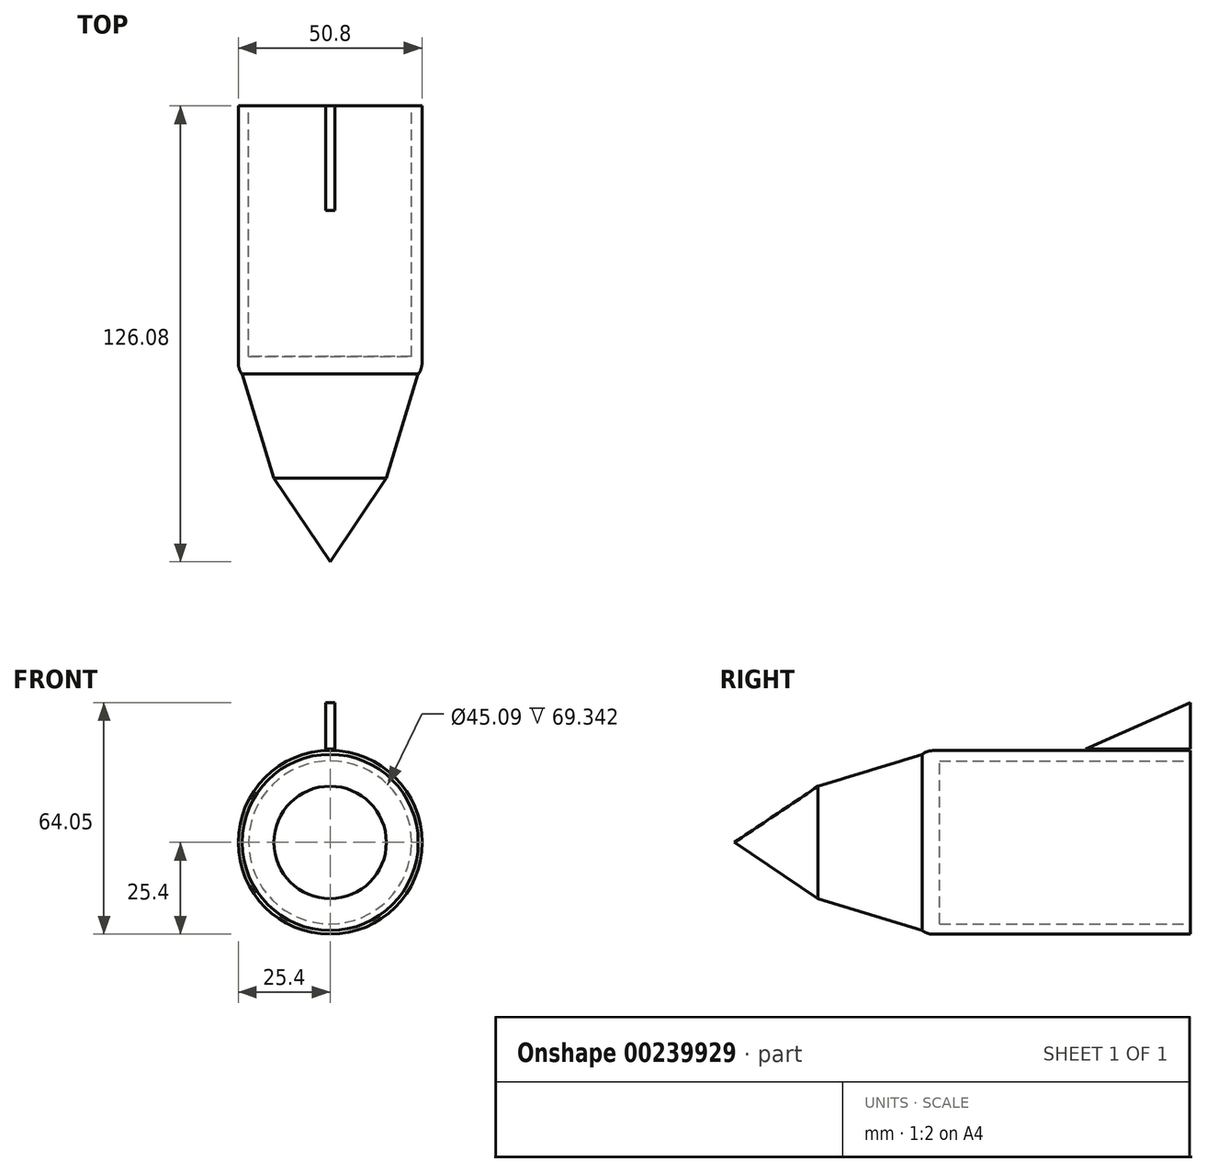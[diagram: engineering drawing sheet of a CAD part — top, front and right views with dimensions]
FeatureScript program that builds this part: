
annotation { "Feature Type Name" : "Feature", "Feature Type Description" : "" }
export const myFeature = defineFeature(function(context is Context, id is Id, definition is map)
    precondition{}
    {
        {
            var Q0;
            Q0=qCreatedBy(makeId("Front.planeOp"),FACE);
            var sketch = newSketch(context, id + "F0", { "sketchPlane" : qUnion([Q0])});
            skCircle(sketch, "E0", {"center": v(0, 0) * mm, "radius": 25.4 * mm});
            skSolve(sketch);
        }
        {
            var Q0;
            Q0 = qSketchRegion(id + "F0", true);
            extrude(context, id + "F1", {"entities" : qUnion([Q0]), "depth" : 76.2 * mm});
        }
        {
            var Q0;
            Q0=qCreatedBy(makeId("Front.planeOp"),FACE);
            var sketch = newSketch(context, id + "F2", { "sketchPlane" : qUnion([Q0])});
            skCircle(sketch, "E1", {"center": v(0, 0) * mm, "radius": 22.55 * mm});
            skSolve(sketch);
        }
        {
            var Q0;
            Q0 = qSketchRegion(id + "F2", true);
            extrude(context, id + "F3", {"entities" : qUnion([Q0]), "operationType" : NewBodyOperationType.REMOVE, "depth" : 69.34 * mm});
        }
        {
            var Q0;
            Q0=makeQuery(id+"F1.opExtrude","CAP_EDGE",EDGE,{"disambiguationData":[OSD([sQuery(id+"F0.wireOp",EDGE,"E0")])],"isStart":false});
            fillet(context, id + "F4", {"entities" : qUnion([Q0]), "radius" : 5.08 * mm, "tangentPropagation" : true, "allowEdgeOverflow" : false});
        }
        {
            var Q0;
            Q0=qCreatedBy(makeId("Right.planeOp"),FACE);
            var sketch = newSketch(context, id + "F5", { "sketchPlane" : qUnion([Q0])});
            skLineSegment(sketch, "E2", {"start": v(-71.31, 0) * mm, "end": v(-126.08, 0) * mm});
            skLineSegment(sketch, "E3", {"start": v(-126.08, 0) * mm, "end": v(-102.97, 15.55) * mm});
            skLineSegment(sketch, "E4", {"start": v(-102.97, 15.55) * mm, "end": v(-71.31, 25.24) * mm});
            skLineSegment(sketch, "E5", {"start": v(-71.31, 25.24) * mm, "end": v(-71.31, 0) * mm});
            skSolve(sketch);
        }
        {
            var Q0;
            Q0=makeQuery(id+"F5.imprint","IMPRINT",FACE,{"disambiguationData":[TD([[makeQuery(id+"F5.imprint","IMPRINT",EDGE,{"derivedFrom":sQuery(id+"F5.wireOp",EDGE,"E2")}),-1.0]])]});
            var Q1;
            Q1=sQuery(id+"F5.wireOp",EDGE,"E2");
            revolve(context, id + "F6", {"operationType" : NewBodyOperationType.ADD, "entities" : qUnion([Q0]), "axis" : qUnion([Q1]), "revolveType" : RevolveType.FULL});
        }
        {
            var Q0;
            Q0=qCreatedBy(makeId("Right.planeOp"),FACE);
            var sketch = newSketch(context, id + "F7", { "sketchPlane" : qUnion([Q0])});
            skLineSegment(sketch, "E6", {"start": v(0, 38.65) * mm, "end": v(-28.93, 25.81) * mm});
            skLineSegment(sketch, "E7", {"start": v(-28.93, 25.81) * mm, "end": v(0, 25.81) * mm});
            skLineSegment(sketch, "E8", {"start": v(0, 25.81) * mm, "end": v(0, 38.65) * mm});
            skSolve(sketch);
        }
        {
            var Q0;
            Q0 = qSketchRegion(id + "F7", true);
            extrude(context, id + "F8", {"entities" : qUnion([Q0]), "endBound" : BoundingType.SYMMETRIC, "depth" : 2.54 * mm});
        }
        {
            var Q0;
            Q0=qCreatedBy(makeId("Right.planeOp"),FACE);
            var sketch = newSketch(context, id + "F9", { "sketchPlane" : qUnion([Q0])});
            skLineSegment(sketch, "E9", {"start": v(0, 0) * mm, "end": v(-70.86, 0) * mm});
            skSolve(sketch);
        }
    });
